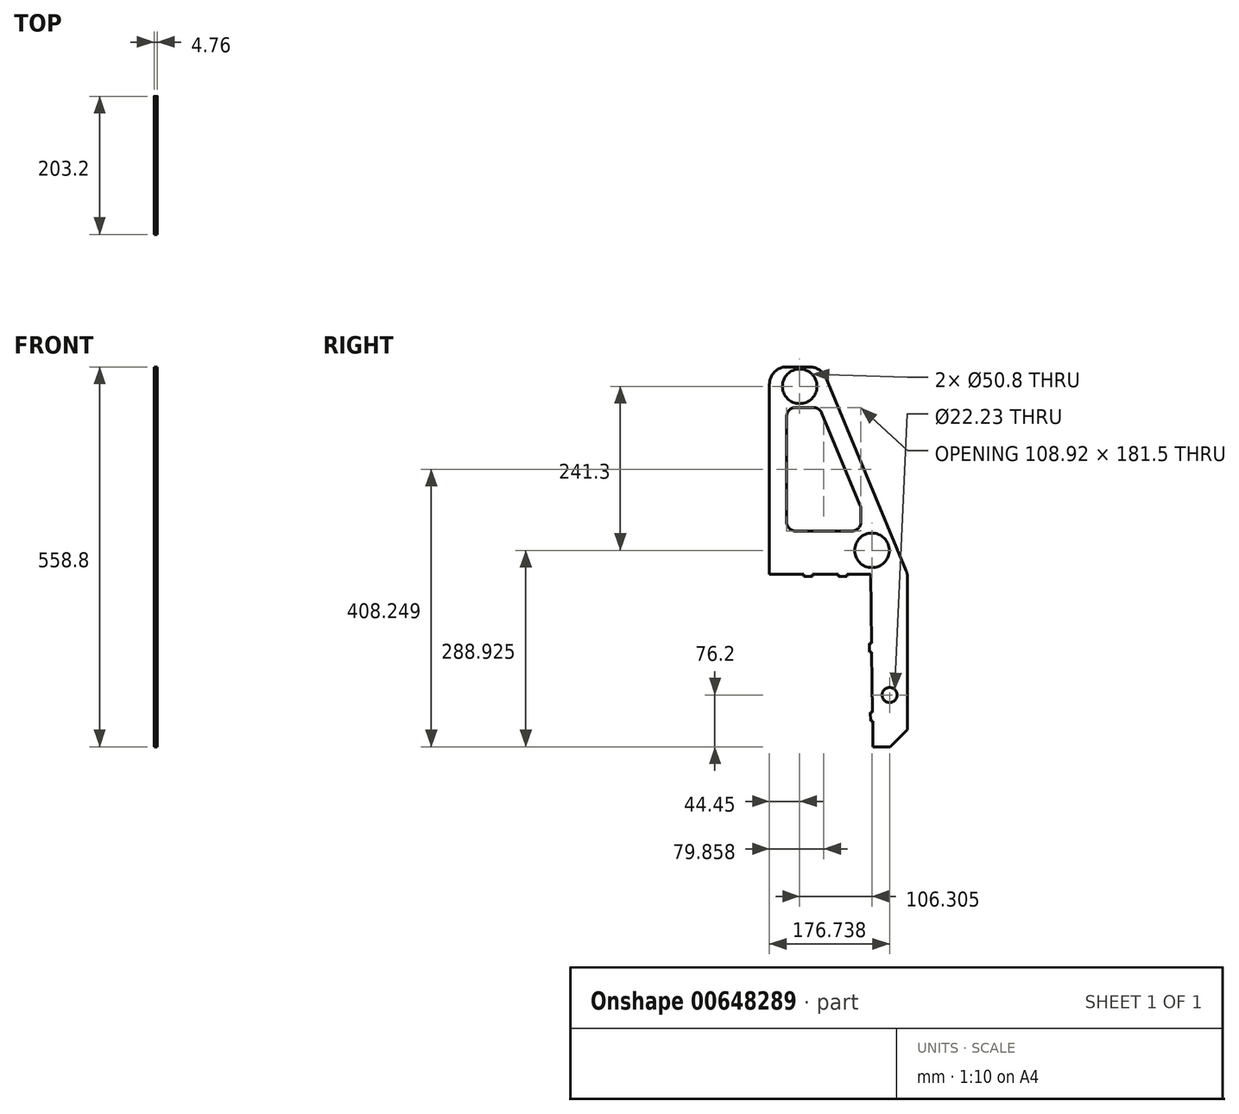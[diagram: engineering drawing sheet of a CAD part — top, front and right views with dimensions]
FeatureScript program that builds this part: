
annotation { "Feature Type Name" : "Feature", "Feature Type Description" : "" }
export const myFeature = defineFeature(function(context is Context, id is Id, definition is map)
    precondition{}
    {
        {
            var Q0;
            Q0=qCreatedBy(makeId("Right.planeOp"),FACE);
            var sketch = newSketch(context, id + "F0", { "sketchPlane" : qUnion([Q0])});
            skLineSegment(sketch, "E0", {"start": v(-54.35, 0) * mm, "end": v(-88.9, 0) * mm});
            skLineSegment(sketch, "E1", {"start": v(-203.2, 0) * mm, "end": v(-203.2, 279.4) * mm});
            skLineSegment(sketch, "E2", {"start": v(-177.8, 304.8) * mm, "end": v(-143.93, 304.8) * mm});
            skLineSegment(sketch, "E3", {"start": v(-120.49, 289.17) * mm, "end": v(-1.95, 4.69) * mm});
            skPoint(sketch, "E4.visualSharp", {"position": v(-203.2, 304.8) * mm});
            skArc(sketch, "E4.filletArc", {"start": v(-177.8, 304.8) * mm, "mid": v(-195.76, 297.36) * mm, "end": v(-203.2, 279.4) * mm});
            skPoint(sketch, "E5.visualSharp", {"position": v(-127, 304.8) * mm});
            skArc(sketch, "E5.filletArc", {"start": v(-120.49, 289.17) * mm, "mid": v(-129.84, 300.53) * mm, "end": v(-143.93, 304.8) * mm});
            skLineSegment(sketch, "E6", {"start": v(0, -5.08) * mm, "end": v(0, -254) * mm});
            skLineSegment(sketch, "E7", {"start": v(0, -254) * mm, "end": v(-50.8, -254) * mm});
            skPoint(sketch, "E8.visualSharp", {"position": v(0, 0) * mm});
            skArc(sketch, "E8.filletArc", {"start": v(0, -5.08) * mm, "mid": v(-0.5, -0.1) * mm, "end": v(-1.95, 4.69) * mm});
            skLineSegment(sketch, "E9", {"start": v(-177.8, 232.3) * mm, "end": v(-177.8, 76.2) * mm});
            skLineSegment(sketch, "E10", {"start": v(-126.34, 237.18) * mm, "end": v(-69.86, 101.63) * mm});
            skLineSegment(sketch, "E11", {"start": v(-68.88, 96.74) * mm, "end": v(-68.88, 76.2) * mm});
            skLineSegment(sketch, "E12", {"start": v(-165.1, 63.5) * mm, "end": v(-81.58, 63.5) * mm});
            skLineSegment(sketch, "E13", {"start": v(-138.07, 245) * mm, "end": v(-165.1, 245) * mm});
            skCircle(sketch, "E14", {"center": v(-158.75, 276.22) * mm, "radius": 25.4 * mm});
            skCircle(sketch, "E15", {"center": v(-52.45, 34.93) * mm, "radius": 25.4 * mm});
            skPoint(sketch, "E16.visualSharp", {"position": v(-177.8, 245) * mm});
            skArc(sketch, "E16.filletArc", {"start": v(-165.1, 245) * mm, "mid": v(-174.08, 241.28) * mm, "end": v(-177.8, 232.3) * mm});
            skPoint(sketch, "E17.visualSharp", {"position": v(-129.6, 245) * mm});
            skArc(sketch, "E17.filletArc", {"start": v(-126.34, 237.18) * mm, "mid": v(-131.02, 242.87) * mm, "end": v(-138.07, 245) * mm});
            skPoint(sketch, "E18.visualSharp", {"position": v(-68.88, 99.28) * mm});
            skArc(sketch, "E18.filletArc", {"start": v(-68.88, 96.74) * mm, "mid": v(-69.13, 99.23) * mm, "end": v(-69.86, 101.63) * mm});
            skPoint(sketch, "E19.visualSharp", {"position": v(-68.88, 63.5) * mm});
            skArc(sketch, "E19.filletArc", {"start": v(-81.58, 63.5) * mm, "mid": v(-72.6, 67.22) * mm, "end": v(-68.88, 76.2) * mm});
            skPoint(sketch, "E20.visualSharp", {"position": v(-177.8, 63.5) * mm});
            skArc(sketch, "E20.filletArc", {"start": v(-177.8, 76.2) * mm, "mid": v(-174.08, 67.22) * mm, "end": v(-165.1, 63.5) * mm});
            skCircle(sketch, "E21", {"center": v(-26.46, -177.8) * mm, "radius": 11.11 * mm});
            skLineSegment(sketch, "E22", {"start": v(-50.8, -254) * mm, "end": v(-51.33, -215.85) * mm});
            skLineSegment(sketch, "E23", {"start": v(-152.4, 0) * mm, "end": v(-152.4, -3.18) * mm});
            skLineSegment(sketch, "E24", {"start": v(-152.4, -3.18) * mm, "end": v(-139.7, -3.18) * mm});
            skLineSegment(sketch, "E25", {"start": v(-139.7, -3.18) * mm, "end": v(-139.7, 0) * mm});
            skLineSegment(sketch, "E26.trimOffspring", {"start": v(-152.4, 0) * mm, "end": v(-203.2, 0) * mm});
            skLineSegment(sketch, "E27", {"start": v(-101.6, 0) * mm, "end": v(-101.6, -3.17) * mm});
            skLineSegment(sketch, "E28", {"start": v(-101.6, -3.17) * mm, "end": v(-88.9, -3.17) * mm});
            skLineSegment(sketch, "E29", {"start": v(-88.9, -3.17) * mm, "end": v(-88.9, 0) * mm});
            skLineSegment(sketch, "E30.trimOffspring", {"start": v(-101.6, 0) * mm, "end": v(-139.7, 0) * mm});
            skLineSegment(sketch, "E31", {"start": v(-52.93, -101.56) * mm, "end": v(-56.1, -101.6) * mm});
            skLineSegment(sketch, "E32", {"start": v(-56.1, -101.6) * mm, "end": v(-55.93, -114.3) * mm});
            skLineSegment(sketch, "E33", {"start": v(-55.93, -114.3) * mm, "end": v(-52.75, -114.25) * mm});
            skLineSegment(sketch, "E34", {"start": v(-51.51, -203.16) * mm, "end": v(-54.69, -203.2) * mm});
            skLineSegment(sketch, "E35", {"start": v(-54.69, -203.2) * mm, "end": v(-54.5, -215.9) * mm});
            skLineSegment(sketch, "E36", {"start": v(-54.5, -215.9) * mm, "end": v(-51.33, -215.85) * mm});
            skLineSegment(sketch, "E37.trimOffspring", {"start": v(-52.93, -101.56) * mm, "end": v(-54.35, 0) * mm});
            skLineSegment(sketch, "E38.trimOffspring", {"start": v(-51.51, -203.16) * mm, "end": v(-52.75, -114.25) * mm});
            skSolve(sketch);
        }
        {
            var Q0;
            Q0=makeQuery(id+"F0.imprint","IMPRINT",FACE,{"disambiguationData":[TD([[makeQuery(id+"F0.imprint","IMPRINT",EDGE,{"derivedFrom":sQuery(id+"F0.wireOp",EDGE,"E0")}),-1.0]])]});
            extrude(context, id + "F1", {"entities" : qUnion([Q0]), "depth" : 4.76 * mm, "offsetDistance" : 25.4 * mm});
        }
        {
            var Q0;
            Q0=makeQuery(id+"F1.opExtrude","SWEPT_EDGE",EDGE,{"disambiguationData":[OSD([sQuery(id+"F0.wireOp",EDGE,"E6"),sQuery(id+"F0.wireOp",EDGE,"E7")])]});
            chamfer(context, id + "F2", {"entities" : qUnion([Q0]), "width" : 25.4 * mm, "tangentPropagation" : true});
        }
    });
